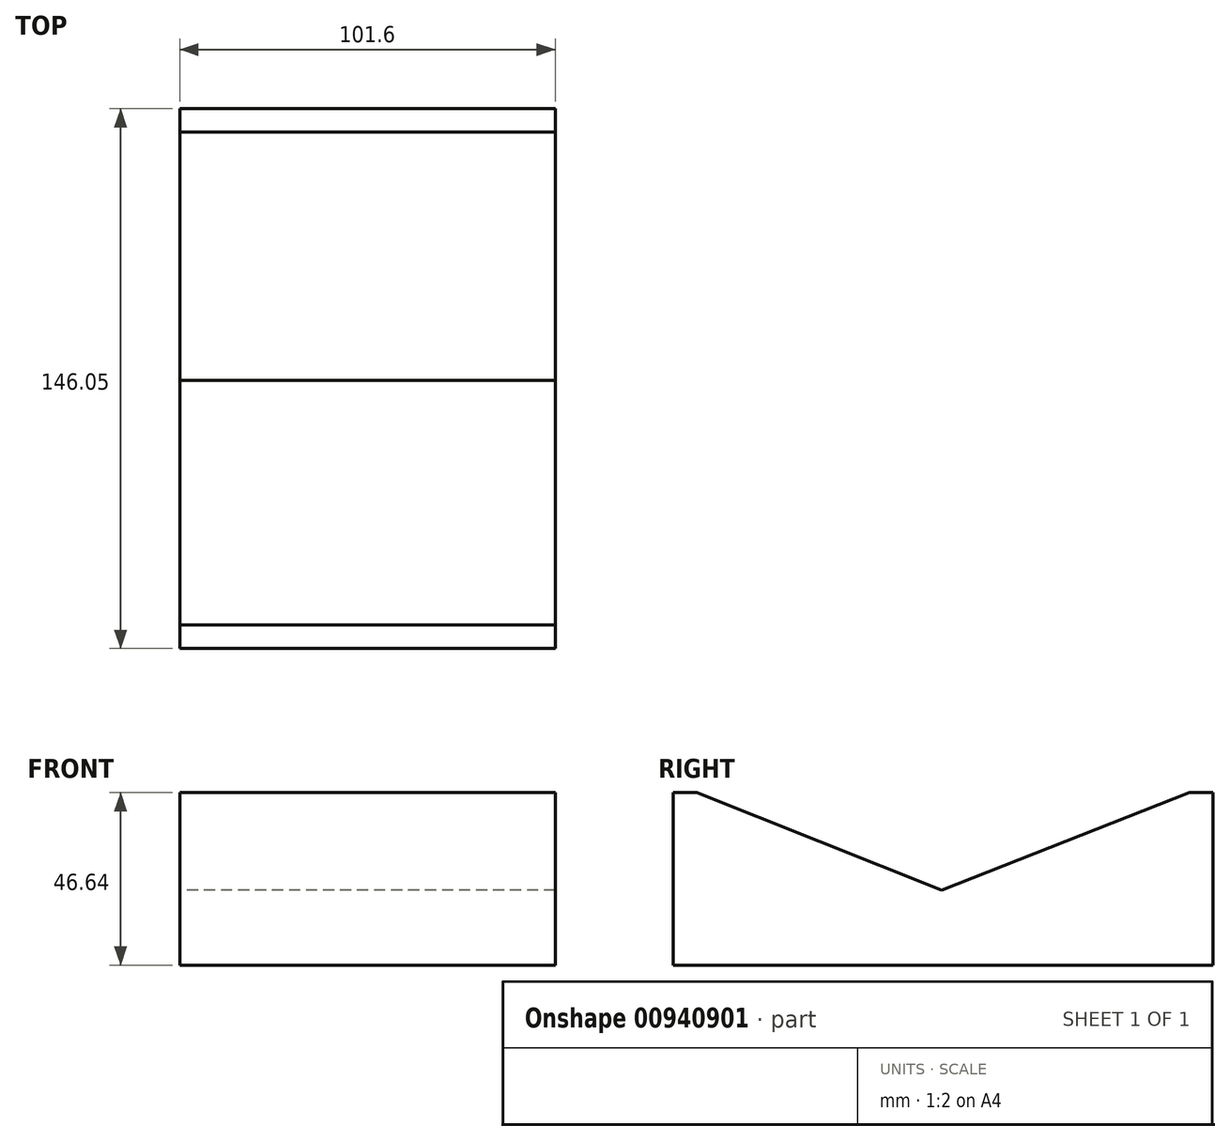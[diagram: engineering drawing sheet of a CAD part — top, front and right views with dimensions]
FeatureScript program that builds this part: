
annotation { "Feature Type Name" : "Feature", "Feature Type Description" : "" }
export const myFeature = defineFeature(function(context is Context, id is Id, definition is map)
    precondition{}
    {
        {
            var Q0;
            Q0=qCreatedBy(makeId("Right.planeOp"),FACE);
            var sketch = newSketch(context, id + "F0", { "sketchPlane" : qUnion([Q0])});
            skLineSegment(sketch, "E0", {"start": v(-66.26, 0) * mm, "end": v(73.44, 0) * mm});
            skLineSegment(sketch, "E1", {"start": v(73.44, 0) * mm, "end": v(73.44, 46.64) * mm});
            skLineSegment(sketch, "E2", {"start": v(73.44, 46.64) * mm, "end": v(67.09, 46.64) * mm});
            skLineSegment(sketch, "E3", {"start": v(67.09, 46.64) * mm, "end": v(0, 20.31) * mm});
            skLineSegment(sketch, "E4", {"start": v(0, 20.31) * mm, "end": v(-66.26, 46.64) * mm});
            skLineSegment(sketch, "E5", {"start": v(-66.26, 46.64) * mm, "end": v(-72.61, 46.64) * mm});
            skLineSegment(sketch, "E6", {"start": v(-72.61, 46.64) * mm, "end": v(-72.61, 0) * mm});
            skLineSegment(sketch, "E7", {"start": v(-72.61, 0) * mm, "end": v(-66.26, 0) * mm});
            skSolve(sketch);
        }
        {
            var Q0;
            Q0 = qSketchRegion(id + "F0", true);
            extrude(context, id + "F1", {"entities" : qUnion([Q0]), "depth" : 101.6 * mm, "offsetDistance" : 25.4 * mm});
        }
    });
